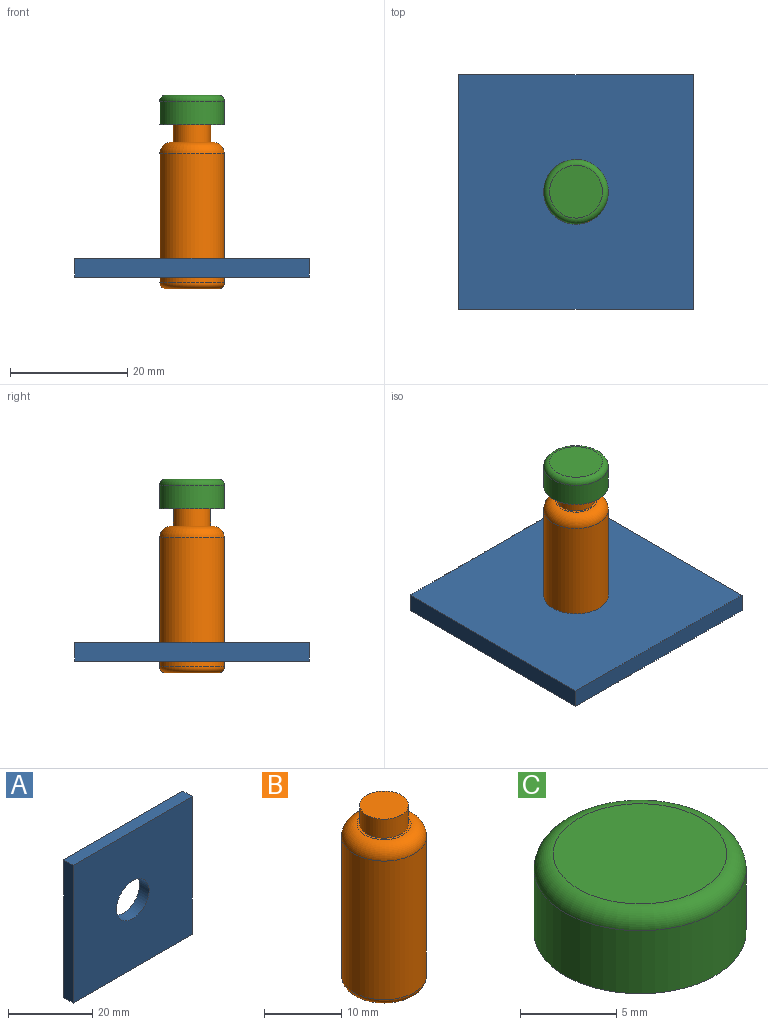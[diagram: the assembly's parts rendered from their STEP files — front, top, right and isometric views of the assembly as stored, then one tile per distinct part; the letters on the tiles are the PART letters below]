
ASSEMBLY  parts=3 mates=4
PART A: 7 faces, bbox 40x3.2x40 mm
  f0: plane 40x3.2mm, normal (-1,0,0), area 128mm2, adj f1,f3,f4,f5
  f1: plane 40x3.2mm, normal (0,0,-1), area 128mm2, adj f0,f2,f4,f5
  f2: plane 40x3.2mm, normal (1,0,0), area 128mm2, adj f1,f3,f4,f5
  f3: plane 40x3.2mm, normal (0,0,1), area 128mm2, adj f0,f2,f4,f5
  f4: plane 40x40mm, normal (0,-1,0), area 1505mm2, adj f0,f1,f2,f3,f6
  f5: plane 40x40mm, normal (0,1,0), area 1505mm2, adj f0,f1,f2,f3,f6
  f6: cylinder r=5.5mm len=11mm, axis (0,-1,0), area 110.6mm2, adj f4,f5
PART B: 7 faces, bbox 11.9x11.9x28 mm
  f0: torus R=4.5mm, axis (0,0,1), area 50.7mm2, adj f1,f6
  f1: cylinder r=5.5mm len=22mm, axis (0,0,1), area 760.3mm2, adj f0,f2
  f2: torus R=3.5mm, axis (0,0,1), area 94.2mm2, adj f1,f3
  f3: plane 7x7mm, normal (0,0,1), area 7mm2, adj f2,f4
  f4: cylinder r=3.17mm len=6.33mm, axis (0,0,1), area 59.7mm2, adj f3,f5
  f5: plane 6.33x6.33mm, normal (0,0,1), area 31.5mm2, adj f4
  f6: plane 9x9mm, normal (0,0,-1), area 63.6mm2, adj f0
PART C: 4 faces, bbox 11.9x11.9x5 mm
  f0: plane 11x11mm, normal (0,0,-1), area 95mm2, adj f1
  f1: cylinder r=5.5mm len=11mm, axis (0,0,1), area 138.2mm2, adj f0,f2
  f2: torus R=4.5mm, axis (0,0,1), area 50.7mm2, adj f1,f3
  f3: plane 9x9mm, normal (0,0,1), area 63.6mm2, adj f2
PLACE A rot(axis=(1,0,0),90deg) t=(-19.34,34.86,-3.61)mm
PLACE B t=(-15.7,19.09,-8.81)mm
PLACE C t=(-15.7,19.09,-8.81)mm
MATE planar A.f6 <-> B.f0  axis (0,0,-1) through (-15.7,19.09,-6.81)mm
MATE fastened C.f1 <-> B.f0  axis (0,0,-1) through (-15.7,19.09,19.19)mm
MATE cylindrical B.f0 <-> C.f1  axis (0,0,1) through (-15.7,19.09,19.19)mm
MATE cylindrical B.f0 <-> A.f6  axis (0,0,-1) through (-15.7,19.09,-8.81)mm
